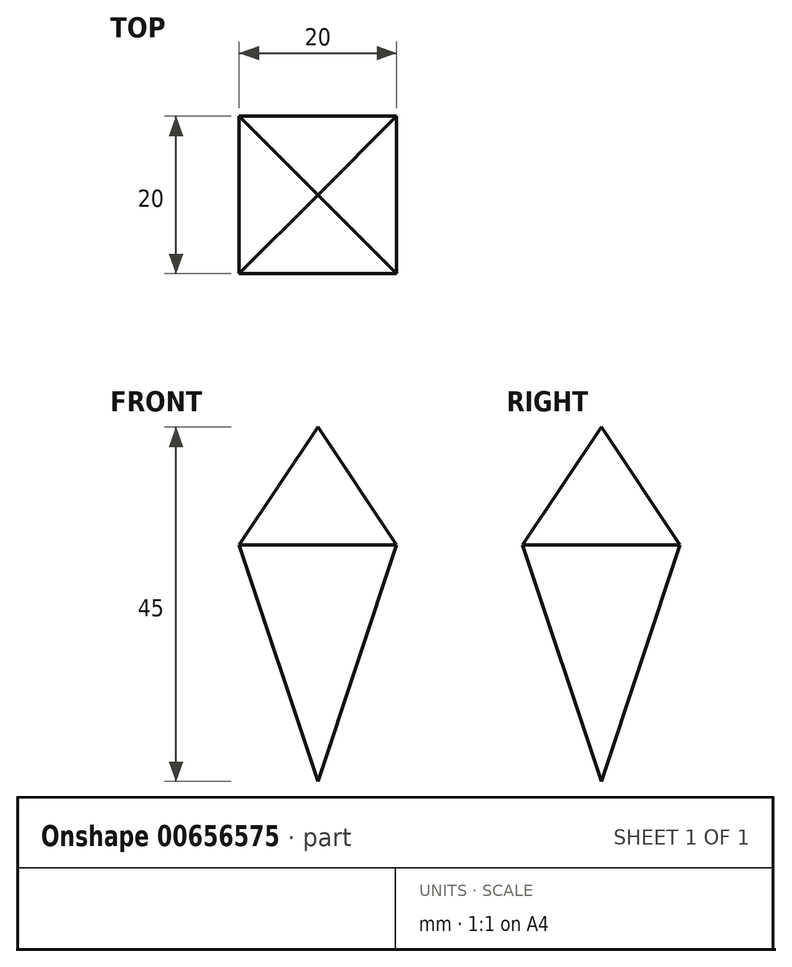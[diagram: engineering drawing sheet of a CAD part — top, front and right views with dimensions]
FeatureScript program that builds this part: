
annotation { "Feature Type Name" : "Feature", "Feature Type Description" : "" }
export const myFeature = defineFeature(function(context is Context, id is Id, definition is map)
    precondition{}
    {
        {
            var Q0;
            Q0=qCreatedBy(makeId("Top.planeOp"),FACE);
            var sketch = newSketch(context, id + "F0", { "sketchPlane" : qUnion([Q0])});
            skLineSegment(sketch, "E0.bottom", {"start": v(-10, 10) * mm, "end": v(10, 10) * mm});
            skLineSegment(sketch, "E0.top", {"start": v(-10, -10) * mm, "end": v(10, -10) * mm});
            skLineSegment(sketch, "E0.left", {"start": v(-10, 10) * mm, "end": v(-10, -10) * mm});
            skLineSegment(sketch, "E0.right", {"start": v(10, 10) * mm, "end": v(10, -10) * mm});
            skPoint(sketch, "E0.middle", {"position": v(0, 0) * mm});
            skSolve(sketch);
        }
        {
            var Q0;
            Q0=qCreatedBy(makeId("Top.planeOp"),FACE);
            cPlane(context, id + "F1", {"entities" : qUnion([Q0]), "cplaneType" : CPlaneType.OFFSET, "offset" : 15 * mm, "width" : 152.4 * mm, "height" : 152.4 * mm});
        }
        {
            var Q0;
            Q0=qCreatedBy(makeId("Top.planeOp"),FACE);
            cPlane(context, id + "F2", {"entities" : qUnion([Q0]), "cplaneType" : CPlaneType.OFFSET, "offset" : 30 * mm, "oppositeDirection" : true, "width" : 152.4 * mm, "height" : 152.4 * mm});
        }
        {
            var Q0;
            Q0=qCreatedBy(id+"F1.planeOp",FACE);
            var sketch = newSketch(context, id + "F3", { "sketchPlane" : qUnion([Q0])});
            skPoint(sketch, "E1", {"position": v(0, 0) * mm});
            skSolve(sketch);
        }
        {
            var Q0;
            Q0=makeQuery(id+"F0.imprint","IMPRINT",FACE,{"disambiguationData":[TD([[makeQuery(id+"F0.imprint","IMPRINT",EDGE,{"derivedFrom":sQuery(id+"F0.wireOp",EDGE,"E0.bottom")}),-1.0]])]});
            var Q1;
            Q1=sQuery(id+"F3.wireOp",VERTEX,"E1");
            loft(context, id + "F4", {"sheetProfilesArray" : [{ "sheetProfileEntities" : qUnion([Q0]) }, { "sheetProfileEntities" : qUnion([Q1]) }]});
        }
        {
            var Q0;
            Q0=qCreatedBy(id+"F2.planeOp",FACE);
            var sketch = newSketch(context, id + "F5", { "sketchPlane" : qUnion([Q0])});
            skPoint(sketch, "E2", {"position": v(0, 0) * mm});
            skSolve(sketch);
        }
        {
            var Q1;
            Q1=makeQuery(id+"F4.opLoft","CAP_FACE",FACE,{"disambiguationData":[OSD([makeQuery(id+"F0.imprint","IMPRINT",FACE,{"disambiguationData":[TD([[makeQuery(id+"F0.imprint","IMPRINT",EDGE,{"derivedFrom":sQuery(id+"F0.wireOp",EDGE,"E0.bottom")}),-1.0]])]})])],"isStart":true});
            var Q2;
            Q2=sQuery(id+"F5.wireOp",VERTEX,"E2");
            loft(context, id + "F6", {"operationType" : NewBodyOperationType.ADD, "sheetProfilesArray" : [{ "sheetProfileEntities" : qUnion([Q1]) }, { "sheetProfileEntities" : qUnion([Q2]) }]});
        }
    });
